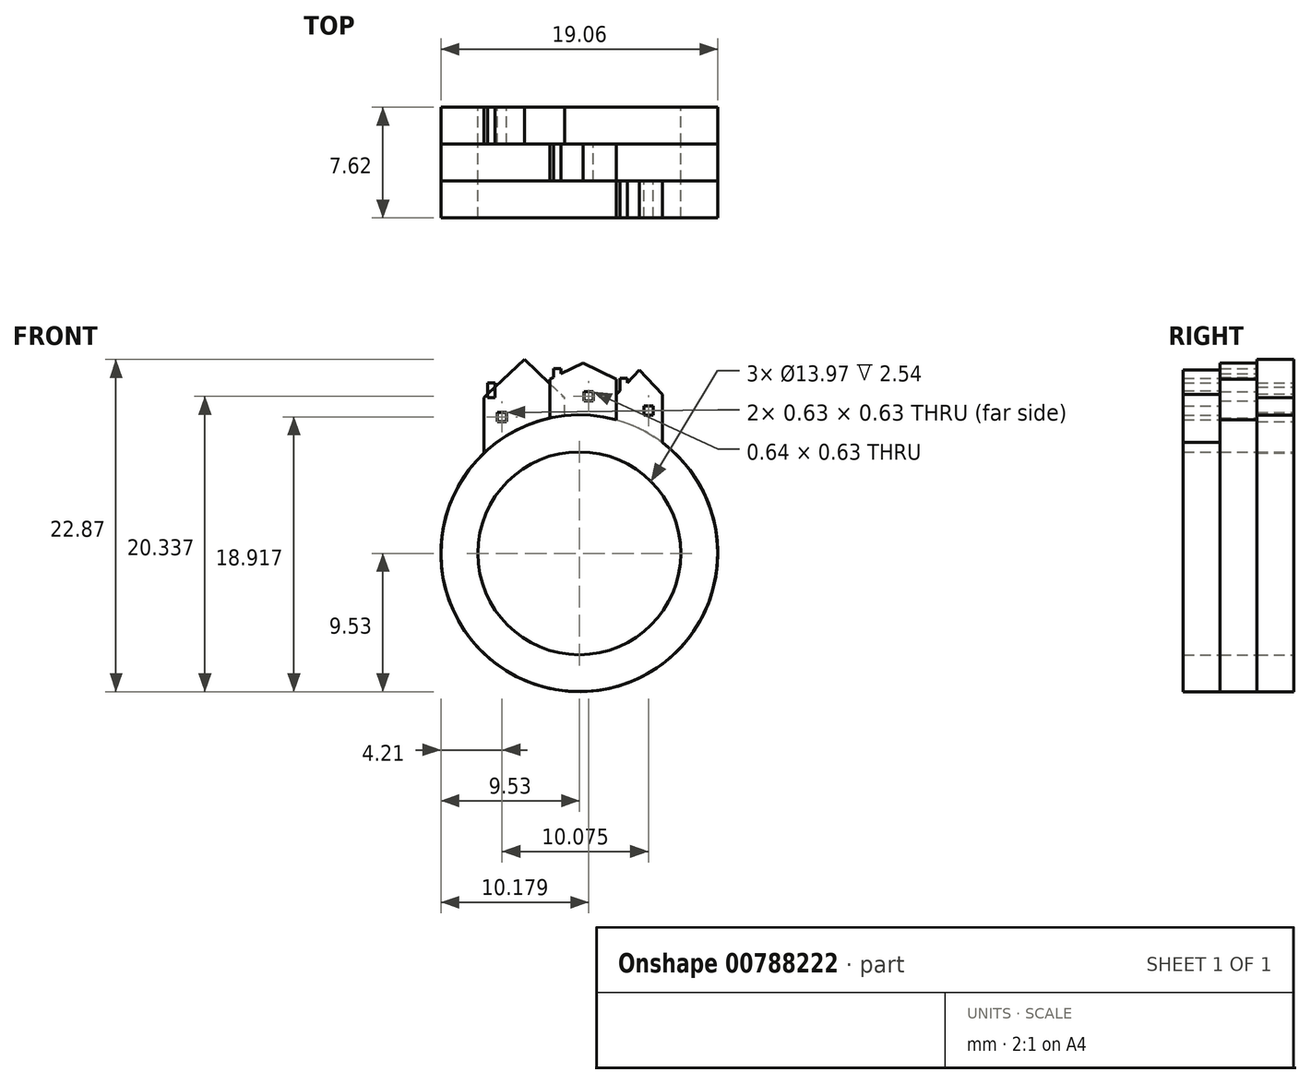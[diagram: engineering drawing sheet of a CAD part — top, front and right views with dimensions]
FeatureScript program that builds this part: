
annotation { "Feature Type Name" : "Feature", "Feature Type Description" : "" }
export const myFeature = defineFeature(function(context is Context, id is Id, definition is map)
    precondition{}
    {
        {
            var Q0;
            Q0=qCreatedBy(makeId("Front.planeOp"),FACE);
            var sketch = newSketch(context, id + "F0", { "sketchPlane" : qUnion([Q0])});
            skCircle(sketch, "E0", {"center": v(0, 0) * mm, "radius": 6.99 * mm});
            skCircle(sketch, "E1", {"center": v(0, 0) * mm, "radius": 9.53 * mm});
            skLineSegment(sketch, "E2.bottom", {"start": v(-6.56, 6.91) * mm, "end": v(-1.02, 6.91) * mm});
            skLineSegment(sketch, "E2.top", {"start": v(-6.56, 10.72) * mm, "end": v(-1.02, 10.72) * mm});
            skLineSegment(sketch, "E2.left", {"start": v(-6.56, 6.91) * mm, "end": v(-6.56, 10.72) * mm});
            skLineSegment(sketch, "E2.right", {"start": v(-1.02, 6.91) * mm, "end": v(-1.02, 10.72) * mm});
            skLineSegment(sketch, "E3", {"start": v(-6.56, 10.72) * mm, "end": v(-3.79, 13.34) * mm});
            skPoint(sketch, "E3.endSnap0", {"position": v(-3.79, 10.72) * mm});
            skLineSegment(sketch, "E4", {"start": v(-3.79, 13.34) * mm, "end": v(-1.02, 10.72) * mm});
            skLineSegment(sketch, "E5.bottom", {"start": v(-5.64, 9.7) * mm, "end": v(-5, 9.7) * mm});
            skLineSegment(sketch, "E5.top", {"start": v(-5.64, 9.07) * mm, "end": v(-5, 9.07) * mm});
            skLineSegment(sketch, "E5.left", {"start": v(-5.64, 9.7) * mm, "end": v(-5.64, 9.07) * mm});
            skLineSegment(sketch, "E5.right", {"start": v(-5, 9.7) * mm, "end": v(-5, 9.07) * mm});
            skPoint(sketch, "E6.oppositeSnap0", {"position": v(-5.17, 12.03) * mm});
            skLineSegment(sketch, "E6.bottom", {"start": v(-6.3, 10.72) * mm, "end": v(-5.8, 10.72) * mm});
            skLineSegment(sketch, "E6.top", {"start": v(-6.3, 11.74) * mm, "end": v(-5.8, 11.74) * mm});
            skLineSegment(sketch, "E6.left", {"start": v(-6.3, 10.72) * mm, "end": v(-6.3, 11.74) * mm});
            skLineSegment(sketch, "E6.right", {"start": v(-5.8, 10.72) * mm, "end": v(-5.8, 11.74) * mm});
            skSolve(sketch);
        }
        {
            var Q0;
            Q0=makeQuery(id+"F0.imprint","IMPRINT",FACE,{"disambiguationData":[TD([[makeQuery(id+"F0.imprint","IMPRINT",EDGE,{"derivedFrom":sQuery(id+"F0.wireOp",EDGE,"E2.top")}),1.0]])]});
            var Q1;
            {var subQ4=sQuery(id+"F0.wireOp",EDGE,"E2.top");Q1=makeQuery(id+"F0.imprint","IMPRINT",FACE,{"disambiguationData":[TD([[makeQuery(id+"F0.imprint","IMPRINT",EDGE,{"derivedFrom":subQ4}),-1.0]])]});}
            var Q2;
            {var subQ0=sQuery(id+"F0.wireOp",EDGE,"E2.bottom");Q2=makeQuery(id+"F0.imprint","IMPRINT",FACE,{"disambiguationData":[TD([[makeQuery(id+"F0.imprint","IMPRINT",EDGE,{"derivedFrom":subQ0}),1.0]])]});}
            var Q3;
            {var subQ0=sQuery(id+"F0.wireOp",EDGE,"E0");Q3=makeQuery(id+"F0.imprint","IMPRINT",FACE,{"disambiguationData":[TD([[makeQuery(id+"F0.imprint","IMPRINT",EDGE,{"derivedFrom":subQ0}),-1.0]])]});}
            var Q4;
            {var subQ5=sQuery(id+"F0.wireOp",EDGE,"E6.top");Q4=makeQuery(id+"F0.imprint","IMPRINT",FACE,{"disambiguationData":[TD([[makeQuery(id+"F0.imprint","IMPRINT",EDGE,{"derivedFrom":subQ5}),-1.0]])]});}
            var Q5;
            {var subQ5=sQuery(id+"F0.wireOp",EDGE,"E6.bottom");Q5=makeQuery(id+"F0.imprint","IMPRINT",FACE,{"disambiguationData":[TD([[makeQuery(id+"F0.imprint","IMPRINT",EDGE,{"derivedFrom":subQ5}),1.0]])]});}
            var Q6;
            {var subQ0=sQuery(id+"F0.wireOp",EDGE,"E4");Q6=makeQuery(id+"F0.imprint","IMPRINT",FACE,{"disambiguationData":[TD([[makeQuery(id+"F0.imprint","IMPRINT",EDGE,{"derivedFrom":subQ0}),-1.0]])]});}
            extrude(context, id + "F1", {"entities" : qUnion([Q0, Q1, Q2, Q3, Q4, Q5, Q6]), "depth" : 2.54 * mm, "offsetDistance" : 25.4 * mm});
        }
        {
            var Q0;
            Q0=makeQuery(id+"F1.opExtrude","CAP_FACE",FACE,{"disambiguationData":[OSD([sQuery(id+"F0.wireOp",EDGE,"E0"),sQuery(id+"F0.wireOp",EDGE,"E1"),sQuery(id+"F0.wireOp",EDGE,"E2.left"),sQuery(id+"F0.wireOp",EDGE,"E2.right"),sQuery(id+"F0.wireOp",EDGE,"E3"),sQuery(id+"F0.wireOp",EDGE,"E4")])],"isStart":false});
            var sketch = newSketch(context, id + "F2", { "sketchPlane" : qUnion([Q0])});
            skCircle(sketch, "E7.1", {"center": v(0, 0) * mm, "radius": 6.99 * mm});
            skCircle(sketch, "E8", {"center": v(0, 0) * mm, "radius": 9.53 * mm});
            skLineSegment(sketch, "E9.bottom", {"start": v(-2.03, 7.16) * mm, "end": v(2.54, 7.16) * mm});
            skLineSegment(sketch, "E9.top", {"start": v(-2.03, 12) * mm, "end": v(2.54, 12) * mm});
            skLineSegment(sketch, "E9.left", {"start": v(-2.03, 7.16) * mm, "end": v(-2.03, 12) * mm});
            skLineSegment(sketch, "E9.right", {"start": v(2.54, 7.16) * mm, "end": v(2.54, 12) * mm});
            skLineSegment(sketch, "E10", {"start": v(-2.03, 12) * mm, "end": v(0.25, 13.1) * mm});
            skPoint(sketch, "E10.endSnap0", {"position": v(0.25, 12) * mm});
            skLineSegment(sketch, "E11", {"start": v(0.25, 13.1) * mm, "end": v(2.54, 12) * mm});
            skLineSegment(sketch, "E12.bottom", {"start": v(0.33, 11.12) * mm, "end": v(0.97, 11.12) * mm});
            skLineSegment(sketch, "E12.top", {"start": v(0.33, 10.49) * mm, "end": v(0.97, 10.49) * mm});
            skLineSegment(sketch, "E12.left", {"start": v(0.33, 11.12) * mm, "end": v(0.33, 10.49) * mm});
            skLineSegment(sketch, "E12.right", {"start": v(0.97, 11.12) * mm, "end": v(0.97, 10.49) * mm});
            skLineSegment(sketch, "E13.bottom", {"start": v(-1.78, 12.11) * mm, "end": v(-1.27, 12.11) * mm});
            skLineSegment(sketch, "E13.top", {"start": v(-1.78, 12.72) * mm, "end": v(-1.27, 12.72) * mm});
            skLineSegment(sketch, "E13.left", {"start": v(-1.78, 12.11) * mm, "end": v(-1.78, 12.72) * mm});
            skLineSegment(sketch, "E13.right", {"start": v(-1.27, 12.11) * mm, "end": v(-1.27, 12.72) * mm});
            skSolve(sketch);
        }
        {
            var Q0;
            Q0=makeQuery(id+"F2.imprint","IMPRINT",FACE,{"disambiguationData":[TD([[makeQuery(id+"F2.imprint","IMPRINT",EDGE,{"derivedFrom":sQuery(id+"F2.wireOp",EDGE,"E7.1")}),-1.0]])]});
            var Q1;
            {var subQ5=sQuery(id+"F2.wireOp",EDGE,"E9.bottom");Q1=makeQuery(id+"F2.imprint","IMPRINT",FACE,{"disambiguationData":[TD([[makeQuery(id+"F2.imprint","IMPRINT",EDGE,{"derivedFrom":subQ5}),1.0]])]});}
            var Q2;
            {var subQ2=sQuery(id+"F2.wireOp",EDGE,"E9.top");Q2=makeQuery(id+"F2.imprint","IMPRINT",FACE,{"disambiguationData":[TD([[makeQuery(id+"F2.imprint","IMPRINT",EDGE,{"derivedFrom":subQ2}),-1.0]])]});}
            var Q3;
            Q3=makeQuery(id+"F2.imprint","IMPRINT",FACE,{"disambiguationData":[TD([[makeQuery(id+"F2.imprint","IMPRINT",EDGE,{"derivedFrom":sQuery(id+"F2.wireOp",EDGE,"E9.top")}),1.0]])]});
            var Q4;
            {var subQ1=makeQuery(id+"F1.opExtrude","CAP_EDGE",EDGE,{"disambiguationData":[OSD([sQuery(id+"F0.wireOp",EDGE,"E2.right")])],"isStart":false});Q4=makeQuery(id+"F2.imprint","IMPRINT",FACE,{"disambiguationData":[TD([[makeQuery(id+"F2.imprint","IMPRINT",EDGE,{"derivedFrom":subQ1}),1.0]])]});}
            var Q5;
            Q5=makeQuery(id+"F2.imprint","IMPRINT",FACE,{"disambiguationData":[TD([[makeQuery(id+"F2.imprint","IMPRINT",EDGE,{"derivedFrom":sQuery(id+"F2.wireOp",EDGE,"E12.bottom")}),1.0]])]});
            var Q6;
            {var subQ0=sQuery(id+"F2.wireOp",EDGE,"E11");Q6=makeQuery(id+"F2.imprint","IMPRINT",FACE,{"disambiguationData":[TD([[makeQuery(id+"F2.imprint","IMPRINT",EDGE,{"derivedFrom":subQ0}),-1.0]])]});}
            var Q7;
            {var subQ5=sQuery(id+"F2.wireOp",EDGE,"E13.top");Q7=makeQuery(id+"F2.imprint","IMPRINT",FACE,{"disambiguationData":[TD([[makeQuery(id+"F2.imprint","IMPRINT",EDGE,{"derivedFrom":subQ5}),-1.0]])]});}
            var Q8;
            {var subQ5=sQuery(id+"F2.wireOp",EDGE,"E13.bottom");Q8=makeQuery(id+"F2.imprint","IMPRINT",FACE,{"disambiguationData":[TD([[makeQuery(id+"F2.imprint","IMPRINT",EDGE,{"derivedFrom":subQ5}),1.0]])]});}
            extrude(context, id + "F3", {"entities" : qUnion([Q0, Q1, Q2, Q3, Q4, Q5, Q6, Q7, Q8]), "depth" : 2.54 * mm, "offsetDistance" : 25.4 * mm});
        }
        {
            var Q0;
            Q0=makeQuery(id+"F3.opExtrude","CAP_FACE",FACE,{"disambiguationData":[OSD([sQuery(id+"F2.wireOp",EDGE,"E7.1"),sQuery(id+"F2.wireOp",EDGE,"E8"),sQuery(id+"F2.wireOp",EDGE,"E9.left"),sQuery(id+"F2.wireOp",EDGE,"E9.right"),sQuery(id+"F2.wireOp",EDGE,"E10"),sQuery(id+"F2.wireOp",EDGE,"E11")])],"isStart":false});
            var sketch = newSketch(context, id + "F4", { "sketchPlane" : qUnion([Q0])});
            skCircle(sketch, "E14.0", {"center": v(0, 0) * mm, "radius": 6.99 * mm});
            skCircle(sketch, "E15", {"center": v(0, 0) * mm, "radius": 9.53 * mm});
            skLineSegment(sketch, "E16.bottom", {"start": v(2.54, 7.63) * mm, "end": v(5.7, 7.63) * mm});
            skLineSegment(sketch, "E16.top", {"start": v(2.54, 10.93) * mm, "end": v(5.7, 10.93) * mm});
            skLineSegment(sketch, "E16.left", {"start": v(2.54, 7.63) * mm, "end": v(2.54, 10.93) * mm});
            skLineSegment(sketch, "E16.right", {"start": v(5.7, 7.63) * mm, "end": v(5.7, 10.93) * mm});
            skLineSegment(sketch, "E17", {"start": v(2.54, 10.93) * mm, "end": v(4.12, 12.6) * mm});
            skPoint(sketch, "E17.endSnap0", {"position": v(4.12, 10.93) * mm});
            skLineSegment(sketch, "E18", {"start": v(4.12, 12.6) * mm, "end": v(5.7, 10.93) * mm});
            skLineSegment(sketch, "E19.bottom", {"start": v(4.44, 10.14) * mm, "end": v(5.07, 10.14) * mm});
            skLineSegment(sketch, "E19.top", {"start": v(4.44, 9.5) * mm, "end": v(5.07, 9.5) * mm});
            skLineSegment(sketch, "E19.left", {"start": v(4.44, 10.14) * mm, "end": v(4.44, 9.5) * mm});
            skLineSegment(sketch, "E19.right", {"start": v(5.07, 10.14) * mm, "end": v(5.07, 9.5) * mm});
            skLineSegment(sketch, "E20.bottom", {"start": v(2.8, 11.04) * mm, "end": v(3.3, 11.04) * mm});
            skLineSegment(sketch, "E20.top", {"start": v(2.8, 12.05) * mm, "end": v(3.3, 12.05) * mm});
            skLineSegment(sketch, "E20.left", {"start": v(2.8, 11.04) * mm, "end": v(2.8, 12.05) * mm});
            skLineSegment(sketch, "E20.right", {"start": v(3.3, 11.04) * mm, "end": v(3.3, 12.05) * mm});
            skSolve(sketch);
        }
        {
            var Q0;
            {var subQ4=sQuery(id+"F4.wireOp",EDGE,"E16.top");Q0=makeQuery(id+"F4.imprint","IMPRINT",FACE,{"disambiguationData":[TD([[makeQuery(id+"F4.imprint","IMPRINT",EDGE,{"derivedFrom":subQ4}),-1.0]])]});}
            var Q1;
            Q1=makeQuery(id+"F4.imprint","IMPRINT",FACE,{"disambiguationData":[TD([[makeQuery(id+"F4.imprint","IMPRINT",EDGE,{"derivedFrom":sQuery(id+"F4.wireOp",EDGE,"E16.top")}),1.0]])]});
            var Q2;
            Q2=makeQuery(id+"F4.imprint","IMPRINT",FACE,{"disambiguationData":[TD([[makeQuery(id+"F4.imprint","IMPRINT",EDGE,{"derivedFrom":sQuery(id+"F4.wireOp",EDGE,"E14.0")}),-1.0]])]});
            var Q3;
            {var subQ3=sQuery(id+"F4.wireOp",EDGE,"E16.bottom");Q3=makeQuery(id+"F4.imprint","IMPRINT",FACE,{"disambiguationData":[TD([[makeQuery(id+"F4.imprint","IMPRINT",EDGE,{"derivedFrom":subQ3}),1.0]])]});}
            var Q4;
            {var subQ5=sQuery(id+"F4.wireOp",EDGE,"E20.bottom");Q4=makeQuery(id+"F4.imprint","IMPRINT",FACE,{"disambiguationData":[TD([[makeQuery(id+"F4.imprint","IMPRINT",EDGE,{"derivedFrom":subQ5}),1.0]])]});}
            var Q5;
            {var subQ5=sQuery(id+"F4.wireOp",EDGE,"E20.top");Q5=makeQuery(id+"F4.imprint","IMPRINT",FACE,{"disambiguationData":[TD([[makeQuery(id+"F4.imprint","IMPRINT",EDGE,{"derivedFrom":subQ5}),-1.0]])]});}
            extrude(context, id + "F5", {"entities" : qUnion([Q0, Q1, Q2, Q3, Q4, Q5]), "depth" : 2.54 * mm, "offsetDistance" : 25.4 * mm});
        }
    });
